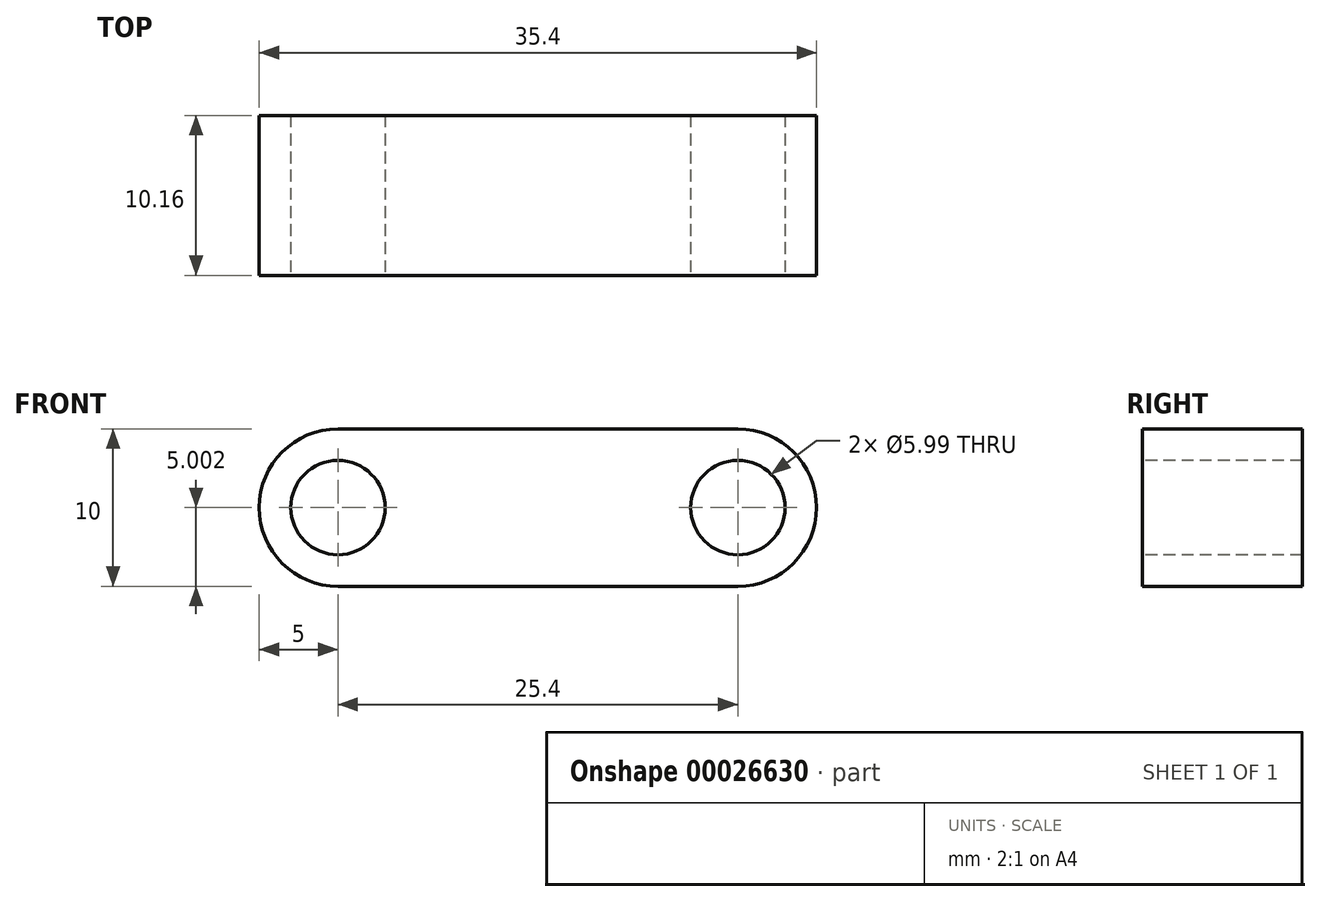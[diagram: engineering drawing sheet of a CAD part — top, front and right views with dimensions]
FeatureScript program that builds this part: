
annotation { "Feature Type Name" : "Feature", "Feature Type Description" : "" }
export const myFeature = defineFeature(function(context is Context, id is Id, definition is map)
    precondition{}
    {
        {
            var Q0;
            Q0=qCreatedBy(makeId("Front.planeOp"),FACE);
            var sketch = newSketch(context, id + "F0", { "sketchPlane" : qUnion([Q0])});
            skLineSegment(sketch, "E0.bottom", {"start": v(-24.3, -3.42) * mm, "end": v(1.1, -3.42) * mm});
            skLineSegment(sketch, "E0.top", {"start": v(-24.3, -13.42) * mm, "end": v(1.1, -13.42) * mm});
            skArc(sketch, "E1", {"start": v(-24.3, -3.42) * mm, "mid": v(-29.3, -8.42) * mm, "end": v(-24.3, -13.42) * mm});
            skArc(sketch, "E2", {"start": v(1.1, -13.42) * mm, "mid": v(6.1, -8.42) * mm, "end": v(1.1, -3.42) * mm});
            skSolve(sketch);
        }
        {
            var Q0;
            Q0=makeQuery(id+"F0.imprint","IMPRINT",FACE,{"disambiguationData":[TD([[makeQuery(id+"F0.imprint","IMPRINT",EDGE,{"derivedFrom":sQuery(id+"F0.wireOp",EDGE,"E0.bottom")}),-1.0]])]});
            extrude(context, id + "F1", {"entities" : qUnion([Q0]), "depth" : 10.16 * mm});
        }
        {
            var Q0;
            Q0=makeQuery(id+"F1.opExtrude","CAP_FACE",FACE,{"disambiguationData":[OSD([sQuery(id+"F0.wireOp",EDGE,"E0.bottom"),sQuery(id+"F0.wireOp",EDGE,"E0.top"),sQuery(id+"F0.wireOp",EDGE,"E1"),sQuery(id+"F0.wireOp",EDGE,"E2")])],"isStart":false});
            var sketch = newSketch(context, id + "F2", { "sketchPlane" : qUnion([Q0])});
            skCircle(sketch, "E3", {"center": v(-24.3, -8.42) * mm, "radius": 3 * mm});
            skCircle(sketch, "E4", {"center": v(1.1, -8.42) * mm, "radius": 3 * mm});
            skSolve(sketch);
        }
        {
            var Q0;
            Q0=makeQuery(id+"F2.imprint","IMPRINT",FACE,{"disambiguationData":[TD([[makeQuery(id+"F2.imprint","IMPRINT",EDGE,{"derivedFrom":sQuery(id+"F2.wireOp",EDGE,"E3")}),1.0]])]});
            var Q1;
            Q1=makeQuery(id+"F2.imprint","IMPRINT",FACE,{"disambiguationData":[TD([[makeQuery(id+"F2.imprint","IMPRINT",EDGE,{"derivedFrom":sQuery(id+"F2.wireOp",EDGE,"E4")}),1.0]])]});
            extrude(context, id + "F3", {"entities" : qUnion([Q0, Q1]), "operationType" : NewBodyOperationType.REMOVE, "oppositeDirection" : true, "depth" : 10.16 * mm});
        }
    });
